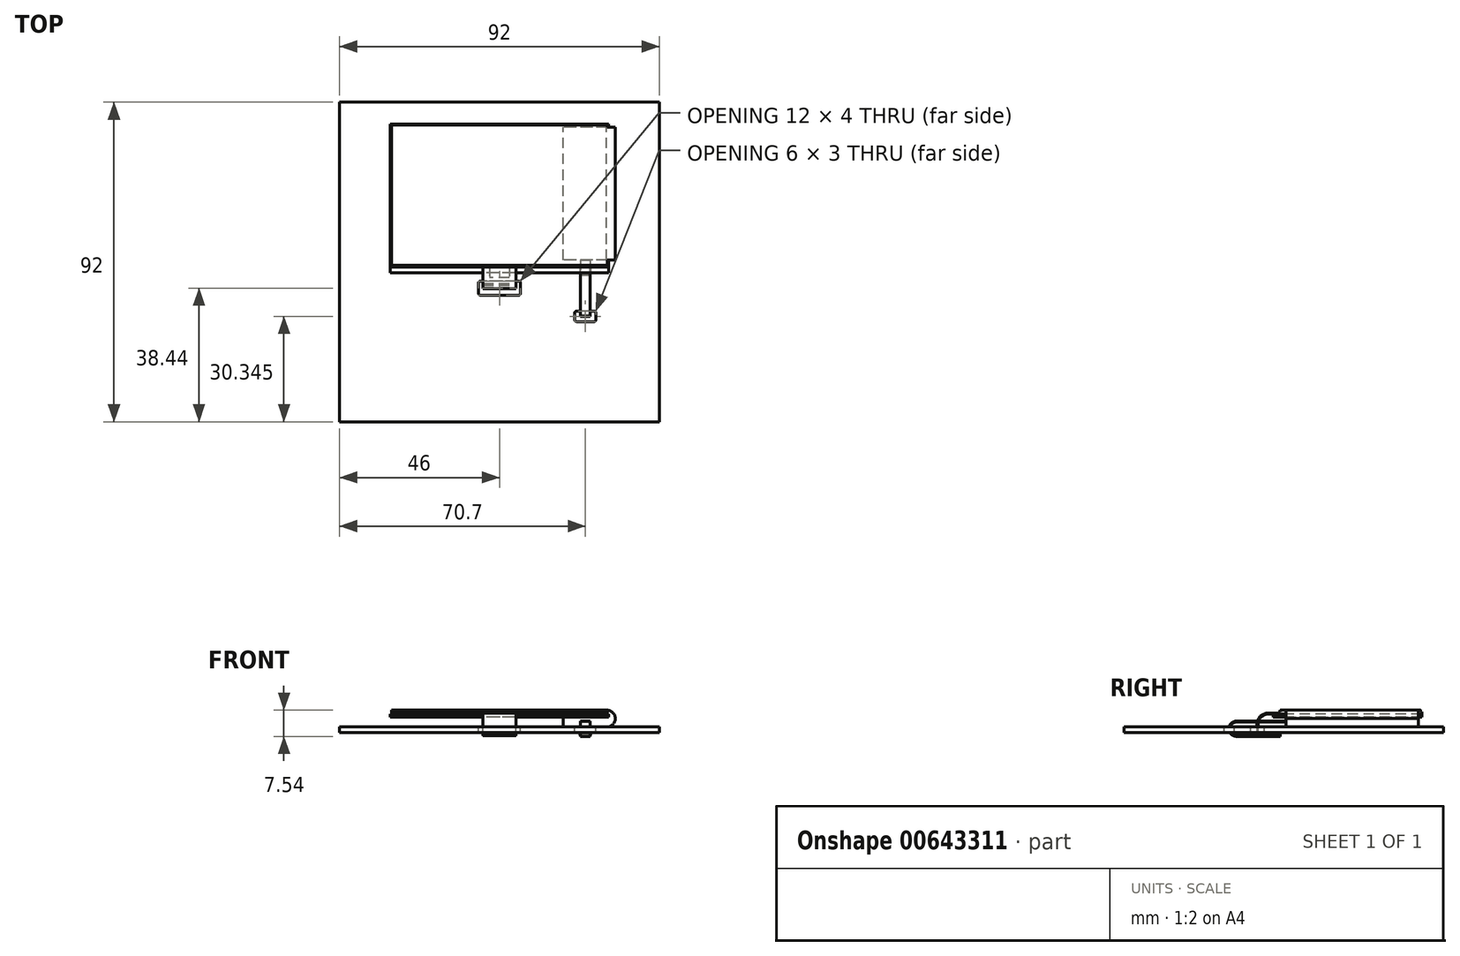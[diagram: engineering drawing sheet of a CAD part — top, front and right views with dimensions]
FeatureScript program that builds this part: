
annotation { "Feature Type Name" : "Feature", "Feature Type Description" : "" }
export const myFeature = defineFeature(function(context is Context, id is Id, definition is map)
    precondition{}
    {
        {
            var Q0;
            Q0=qCreatedBy(makeId("Top.planeOp"),FACE);
            var sketch = newSketch(context, id + "F0", { "sketchPlane" : qUnion([Q0])});
            skLineSegment(sketch, "E0.bottom", {"start": v(31.4, 21.41) * mm, "end": v(-31.4, 21.41) * mm});
            skLineSegment(sketch, "E0.top", {"start": v(31.4, -21.41) * mm, "end": v(-31.4, -21.41) * mm});
            skLineSegment(sketch, "E0.left", {"start": v(31.4, 21.41) * mm, "end": v(31.4, -21.41) * mm});
            skLineSegment(sketch, "E0.right", {"start": v(-31.4, 21.41) * mm, "end": v(-31.4, -21.41) * mm});
            skPoint(sketch, "E0.middle", {"position": v(0, 0) * mm});
            skSolve(sketch);
        }
        {
            var Q0;
            Q0=makeQuery(id+"F0.imprint","IMPRINT",FACE,{"disambiguationData":[TD([[makeQuery(id+"F0.imprint","IMPRINT",EDGE,{"derivedFrom":sQuery(id+"F0.wireOp",EDGE,"E0.bottom")}),1.0]])]});
            extrude(context, id + "F1", {"entities" : qUnion([Q0]), "depth" : (0.7 + 0.1) * mm, "offsetDistance" : 25 * mm});
        }
        {
            var Q0;
            Q0=makeQuery(id+"F1.opExtrude","CAP_FACE",FACE,{"disambiguationData":[OSD([sQuery(id+"F0.wireOp",EDGE,"E0.bottom"),sQuery(id+"F0.wireOp",EDGE,"E0.top"),sQuery(id+"F0.wireOp",EDGE,"E0.left"),sQuery(id+"F0.wireOp",EDGE,"E0.right")])],"isStart":true});
            var sketch = newSketch(context, id + "F2", { "sketchPlane" : qUnion([Q0])});
            skLineSegment(sketch, "E1.bottom", {"start": v(33.35, 17.74) * mm, "end": v(18.35, 17.74) * mm});
            skLineSegment(sketch, "E1.top", {"start": v(33.35, -20.41) * mm, "end": v(18.35, -20.41) * mm});
            skLineSegment(sketch, "E1.left", {"start": v(33.35, 17.74) * mm, "end": v(33.35, -20.41) * mm});
            skLineSegment(sketch, "E1.right", {"start": v(18.35, 17.74) * mm, "end": v(18.35, -20.41) * mm});
            skSolve(sketch);
        }
        {
            var Q0;
            Q0 = qSketchRegion(id + "F2", true);
            extrude(context, id + "F3", {"entities" : qUnion([Q0]), "operationType" : NewBodyOperationType.ADD, "depth" : 2.9 * mm, "offsetDistance" : 25 * mm});
        }
        {
            var Q0;
            {var subQ0=sQuery(id+"F0.wireOp",EDGE,"E0.right");var subQ1=sQuery(id+"F0.wireOp",EDGE,"E0.left");var subQ2=sQuery(id+"F0.wireOp",EDGE,"E0.top");var subQ3=sQuery(id+"F0.wireOp",EDGE,"E0.bottom");Q0=makeQuery(id+"FSjtb73LsPTqSAc_1.boolean.opBoolean","MERGE",FACE,{"derivedFrom":[makeQuery(id+"F1.opExtrude","CAP_FACE",FACE,{"disambiguationData":[OSD([subQ3,subQ2,subQ1,subQ0])],"isStart":false}),makeQuery(id+"FSjtb73LsPTqSAc_1.opExtrude","CAP_FACE",FACE,{"disambiguationData":[OSD([subQ3,subQ2,subQ1,subQ0])],"isStart":false})]});}
            var sketch = newSketch(context, id + "F4", { "sketchPlane" : qUnion([Q0])});
            skLineSegment(sketch, "E2.bottom", {"start": v(-31, 21.4) * mm, "end": v(31, 21.41) * mm});
            skLineSegment(sketch, "E2.top", {"start": v(-31, -19.81) * mm, "end": v(31, -19.81) * mm});
            skLineSegment(sketch, "E2.left", {"start": v(-31, 21.4) * mm, "end": v(-31, -19.81) * mm});
            skLineSegment(sketch, "E2.right", {"start": v(31, 21.41) * mm, "end": v(31, -19.81) * mm});
            skLineSegment(sketch, "E3", {"start": v(0, 21.4) * mm, "end": v(0, -19.81) * mm, "construction": true});
            skSolve(sketch);
        }
        {
            var Q0;
            Q0=makeQuery(id+"F4.imprint","IMPRINT",FACE,{"disambiguationData":[TD([[makeQuery(id+"F4.imprint","IMPRINT",EDGE,{"derivedFrom":sQuery(id+"F4.wireOp",EDGE,"E2.bottom")}),1.0]])]});
            extrude(context, id + "F5", {"entities" : qUnion([Q0]), "operationType" : NewBodyOperationType.ADD, "depth" : 0.6 * mm, "offsetDistance" : 25 * mm});
        }
        {
            var Q0;
            Q0=makeQuery(id+"F5.opExtrude","CAP_FACE",FACE,{"disambiguationData":[OSD([sQuery(id+"F4.wireOp",EDGE,"E2.bottom"),sQuery(id+"F4.wireOp",EDGE,"E2.top"),sQuery(id+"F4.wireOp",EDGE,"E2.left"),sQuery(id+"F4.wireOp",EDGE,"E2.right")])],"isStart":false});
            var sketch = newSketch(context, id + "F6", { "sketchPlane" : qUnion([Q0])});
            skLineSegment(sketch, "E4.bottom", {"start": v(-31, 21.11) * mm, "end": v(31, 21.11) * mm});
            skLineSegment(sketch, "E4.top", {"start": v(-31, -19.31) * mm, "end": v(31, -19.31) * mm});
            skLineSegment(sketch, "E4.left", {"start": v(-31, 21.11) * mm, "end": v(-31, -19.31) * mm});
            skLineSegment(sketch, "E4.right", {"start": v(31, 21.11) * mm, "end": v(31, -19.31) * mm});
            skLineSegment(sketch, "E5", {"start": v(0, 21.11) * mm, "end": v(0, -19.31) * mm, "construction": true});
            skSolve(sketch);
        }
        {
            var Q0;
            Q0=makeQuery(id+"F6.imprint","IMPRINT",FACE,{"disambiguationData":[TD([[makeQuery(id+"F6.imprint","IMPRINT",EDGE,{"derivedFrom":sQuery(id+"F6.wireOp",EDGE,"E4.bottom")}),-1.0]])]});
            extrude(context, id + "F7", {"entities" : qUnion([Q0]), "operationType" : NewBodyOperationType.ADD, "depth" : (1.95 - 1.41) * mm, "offsetDistance" : 25 * mm});
        }
        {
            var Q0;
            Q0=makeQuery(id+"F7.opExtrude","CAP_FACE",FACE,{"disambiguationData":[OSD([sQuery(id+"F6.wireOp",EDGE,"E4.bottom"),sQuery(id+"F6.wireOp",EDGE,"E4.top"),sQuery(id+"F6.wireOp",EDGE,"E4.left"),sQuery(id+"F6.wireOp",EDGE,"E4.right")])],"isStart":false});
            var sketch = newSketch(context, id + "F8", { "sketchPlane" : qUnion([Q0])});
            skLineSegment(sketch, "E6.bottom", {"start": v(33.35, 20.41) * mm, "end": v(-31, 20.4) * mm});
            skLineSegment(sketch, "E6.top", {"start": v(33.35, -17.74) * mm, "end": v(-31, -17.74) * mm});
            skLineSegment(sketch, "E6.left", {"start": v(-31, 20.41) * mm, "end": v(-31, -17.74) * mm});
            skLineSegment(sketch, "E6.right", {"start": v(33.35, 20.41) * mm, "end": v(33.35, -17.74) * mm});
            skSolve(sketch);
        }
        {
            var Q0;
            Q0=makeQuery(id+"F8.imprint","IMPRINT",FACE,{"disambiguationData":[TD([[makeQuery(id+"F8.imprint","IMPRINT",EDGE,{"derivedFrom":sQuery(id+"F8.wireOp",EDGE,"E6.bottom")}),1.0]])]});
            var Q1;
            Q1=makeQuery(id+"F3.opExtrude","CAP_FACE",FACE,{"disambiguationData":[OSD([sQuery(id+"F2.wireOp",EDGE,"E1.bottom"),sQuery(id+"F2.wireOp",EDGE,"E1.top"),sQuery(id+"F2.wireOp",EDGE,"E1.left"),sQuery(id+"F2.wireOp",EDGE,"E1.right")])],"isStart":true});
            extrude(context, id + "F9", {"entities" : qUnion([Q0]), "operationType" : NewBodyOperationType.ADD, "endBound" : BoundingType.UP_TO_SURFACE, "oppositeDirection" : true, "depth" : 25 * mm, "endBoundEntityFace" : qUnion([Q1]), "offsetDistance" : 25 * mm});
        }
        {
            var Q0;
            Q0=makeQuery(id+"F9.opExtrude","CAP_EDGE",EDGE,{"disambiguationData":[OSD([sQuery(id+"F8.wireOp",EDGE,"E6.right")])],"isStart":true});
            var Q1;
            Q1=makeQuery(id+"F3.opExtrude","CAP_EDGE",EDGE,{"disambiguationData":[OSD([sQuery(id+"F2.wireOp",EDGE,"E1.left")])],"isStart":false});
            fillet(context, id + "F10", {"entities" : qUnion([Q0, Q1]), "radius" : 2.5 * mm, "tangentPropagation" : true, "allowEdgeOverflow" : false});
        }
        {
            var Q0;
            Q0=makeQuery(id+"F9.boolean.opBoolean","MERGE",FACE,{"derivedFrom":[makeQuery(id+"F3.opExtrude","SWEPT_FACE",FACE,{"disambiguationData":[OSD([sQuery(id+"F2.wireOp",EDGE,"E1.bottom")])]}),makeQuery(id+"F9.opExtrude","SWEPT_FACE",FACE,{"disambiguationData":[OSD([sQuery(id+"F8.wireOp",EDGE,"E6.top")])]})]});
            var sketch = newSketch(context, id + "F11", { "sketchPlane" : qUnion([Q0])});
            skLineSegment(sketch, "E7.bottom", {"start": v(23.3, -1.2) * mm, "end": v(26.1, -1.2) * mm});
            skLineSegment(sketch, "E7.top", {"start": v(23.3, -1.5) * mm, "end": v(26.1, -1.5) * mm});
            skLineSegment(sketch, "E7.left", {"start": v(23.3, -1.2) * mm, "end": v(23.3, -1.5) * mm});
            skLineSegment(sketch, "E7.right", {"start": v(26.1, -1.2) * mm, "end": v(26.1, -1.5) * mm});
            skPoint(sketch, "E8", {"position": v(24.7, -1.35) * mm});
            skLineSegment(sketch, "E9", {"start": v(24.7, -1.2) * mm, "end": v(24.7, -1.35) * mm, "construction": true});
            skLineSegment(sketch, "E10", {"start": v(24.7, -1.35) * mm, "end": v(26.1, -1.35) * mm, "construction": true});
            skSolve(sketch);
        }
        {
            var Q0;
            Q0=makeQuery(id+"F5.opExtrude","SWEPT_FACE",FACE,{"disambiguationData":[OSD([sQuery(id+"F4.wireOp",EDGE,"E2.top")])]});
            var sketch = newSketch(context, id + "F12", { "sketchPlane" : qUnion([Q0])});
            skLineSegment(sketch, "E11.bottom", {"start": v(4.75, 1.1) * mm, "end": v(-4.75, 1.1) * mm});
            skLineSegment(sketch, "E11.top", {"start": v(4.75, 0.81) * mm, "end": v(-4.75, 0.8) * mm});
            skLineSegment(sketch, "E11.left", {"start": v(4.75, 1.1) * mm, "end": v(4.75, 0.8) * mm});
            skLineSegment(sketch, "E11.right", {"start": v(-4.75, 1.1) * mm, "end": v(-4.75, 0.81) * mm});
            skPoint(sketch, "E11.middle", {"position": v(0, 0.96) * mm});
            skPoint(sketch, "E11.middle.positionSnap0", {"position": v(0, 0.8) * mm});
            skPoint(sketch, "E11.centerSnap0", {"position": v(0, 0.8) * mm});
            skSolve(sketch);
        }
        {
            var Q0;
            Q0=makeQuery(id+"F3.opExtrude","CAP_FACE",FACE,{"disambiguationData":[OSD([sQuery(id+"F2.wireOp",EDGE,"E1.bottom"),sQuery(id+"F2.wireOp",EDGE,"E1.top"),sQuery(id+"F2.wireOp",EDGE,"E1.left"),sQuery(id+"F2.wireOp",EDGE,"E1.right")])],"isStart":false});
            var sketch = newSketch(context, id + "F13", { "sketchPlane" : qUnion([Q0])});
            skLineSegment(sketch, "E12.bottom", {"start": v(46, 64.33) * mm, "end": v(-46, 64.33) * mm});
            skLineSegment(sketch, "E12.top", {"start": v(46, -27.67) * mm, "end": v(-46, -27.67) * mm});
            skLineSegment(sketch, "E12.left", {"start": v(46, 64.33) * mm, "end": v(46, -27.67) * mm});
            skLineSegment(sketch, "E12.right", {"start": v(-46, 64.33) * mm, "end": v(-46, -27.67) * mm});
            skPoint(sketch, "E12.middle", {"position": v(0, 64.33) * mm});
            skSolve(sketch);
        }
        {
            var Q0;
            Q0 = qSketchRegion(id + "F13", true);
            extrude(context, id + "F14", {"entities" : qUnion([Q0]), "depth" : 1.6 * mm, "offsetDistance" : 25 * mm});
        }
        {
            var Q0;
            Q0=makeQuery(id+"F14.opExtrude","CAP_FACE",FACE,{"disambiguationData":[OSD([sQuery(id+"F13.wireOp",EDGE,"E12.bottom"),sQuery(id+"F13.wireOp",EDGE,"E12.top"),sQuery(id+"F13.wireOp",EDGE,"E12.left"),sQuery(id+"F13.wireOp",EDGE,"E12.right")])],"isStart":false});
            var sketch = newSketch(context, id + "F15", { "sketchPlane" : qUnion([Q0])});
            skPoint(sketch, "E13", {"position": v(24.7, 21.74) * mm});
            skSolve(sketch);
        }
        {
            var Q0;
            {var subQ3=sQuery(id+"F13.wireOp",EDGE,"E12.bottom");Q0=makeQuery(id+"F15.imprint","IMPRINT",FACE,{"disambiguationData":[TD([[makeQuery(id+"F15.imprint","IMPRINT",EDGE,{"derivedFrom":makeQuery(id+"F14.opExtrude","CAP_EDGE",EDGE,{"disambiguationData":[OSD([subQ3])],"isStart":false})}),1.0]])]});}
            var sketch = newSketch(context, id + "F16", { "sketchPlane" : qUnion([Q0])});
            skLineSegment(sketch, "E14.bottom", {"start": v(26.2, 19.35) * mm, "end": v(23.2, 19.35) * mm});
            skLineSegment(sketch, "E14.top", {"start": v(26.2, 22.25) * mm, "end": v(23.2, 22.25) * mm});
            skLineSegment(sketch, "E14.left", {"start": v(26.2, 19.35) * mm, "end": v(26.2, 22.25) * mm});
            skLineSegment(sketch, "E14.right", {"start": v(23.2, 19.35) * mm, "end": v(23.2, 22.25) * mm});
            skPoint(sketch, "E14.middle", {"position": v(24.7, 20.8) * mm});
            skSolve(sketch);
        }
        {
            var Q0;
            Q0=makeQuery(id+"F16.imprint","IMPRINT",FACE,{"disambiguationData":[TD([[makeQuery(id+"F16.imprint","IMPRINT",EDGE,{"derivedFrom":sQuery(id+"F16.wireOp",EDGE,"E14.bottom")}),-1.0]])]});
            extrude(context, id + "F17", {"entities" : qUnion([Q0]), "operationType" : NewBodyOperationType.ADD, "depth" : 0.79 * mm, "offsetDistance" : 25 * mm});
        }
        {
            var Q0;
            Q0=makeQuery(id+"F14.opExtrude","SWEPT_FACE",FACE,{"disambiguationData":[OSD([sQuery(id+"F13.wireOp",EDGE,"E12.right")])]});
            cPlane(context, id + "F18", {"entities" : qUnion([Q0]), "cplaneType" : CPlaneType.OFFSET, "offset" : (70.7) * mm, "oppositeDirection" : true, "width" : 150 * mm, "height" : 150 * mm});
        }
        {
            var Q0;
            Q0=qCreatedBy(id+"F18.planeOp",FACE);
            var sketch = newSketch(context, id + "F19", { "sketchPlane" : qUnion([Q0])});
            skLineSegment(sketch, "E15", {"start": v(17.74, -1.35) * mm, "end": v(31.94, -1.35) * mm});
            skArc(sketch, "E16", {"start": v(31.94, -5.44) * mm, "mid": v(33.98, -3.4) * mm, "end": v(31.94, -1.35) * mm});
            skLineSegment(sketch, "E17", {"start": v(31.94, -5.44) * mm, "end": v(19.35, -5.44) * mm});
            skSolve(sketch);
        }
        {
            var Q0;
            Q0 = qSketchRegion(id + "F11", true);
            var Q1;
            Q1 = qConstructionFilter(qBodyType(qCreatedBy(id + "F19" ,EDGE), BodyType.WIRE), ConstructionObject.NO);
            sweep(context, id + "F20", {"operationType" : NewBodyOperationType.ADD, "profiles" : qUnion([Q0]), "path" : qUnion([Q1])});
        }
        {
            var Q0;
            Q0=makeQuery(id+"F14.opExtrude","CAP_FACE",FACE,{"disambiguationData":[OSD([sQuery(id+"F13.wireOp",EDGE,"E12.bottom"),sQuery(id+"F13.wireOp",EDGE,"E12.top"),sQuery(id+"F13.wireOp",EDGE,"E12.left"),sQuery(id+"F13.wireOp",EDGE,"E12.right")])],"isStart":true});
            var sketch = newSketch(context, id + "F21", { "sketchPlane" : qUnion([Q0])});
            skLineSegment(sketch, "E18.bottom", {"start": v(27.3, -32.48) * mm, "end": v(22.1, -32.48) * mm});
            skLineSegment(sketch, "E18.top", {"start": v(27.3, -35.48) * mm, "end": v(22.1, -35.48) * mm});
            skLineSegment(sketch, "E18.left", {"start": v(27.7, -32.88) * mm, "end": v(27.7, -35.08) * mm});
            skLineSegment(sketch, "E18.right", {"start": v(21.7, -32.88) * mm, "end": v(21.7, -35.08) * mm});
            skPoint(sketch, "E18.middle", {"position": v(24.7, -33.98) * mm});
            skPoint(sketch, "E19.visualSharp", {"position": v(21.7, -32.48) * mm});
            skArc(sketch, "E19.filletArc", {"start": v(22.1, -32.48) * mm, "mid": v(21.82, -32.6) * mm, "end": v(21.7, -32.88) * mm});
            skPoint(sketch, "E20.visualSharp", {"position": v(27.7, -32.48) * mm});
            skArc(sketch, "E20.filletArc", {"start": v(27.7, -32.88) * mm, "mid": v(27.58, -32.6) * mm, "end": v(27.3, -32.48) * mm});
            skPoint(sketch, "E21.visualSharp", {"position": v(27.7, -35.48) * mm});
            skArc(sketch, "E21.filletArc", {"start": v(27.3, -35.48) * mm, "mid": v(27.58, -35.37) * mm, "end": v(27.7, -35.08) * mm});
            skPoint(sketch, "E22.visualSharp", {"position": v(21.7, -35.48) * mm});
            skArc(sketch, "E22.filletArc", {"start": v(21.7, -35.08) * mm, "mid": v(21.82, -35.37) * mm, "end": v(22.1, -35.48) * mm});
            skSolve(sketch);
        }
        {
            var Q0;
            Q0 = qSketchRegion(id + "F21", true);
            var Q1;
            Q1=makeQuery(id+"F14.opExtrude","CAP_FACE",FACE,{"disambiguationData":[OSD([sQuery(id+"F13.wireOp",EDGE,"E12.bottom"),sQuery(id+"F13.wireOp",EDGE,"E12.top"),sQuery(id+"F13.wireOp",EDGE,"E12.left"),sQuery(id+"F13.wireOp",EDGE,"E12.right")])],"isStart":false});
            extrude(context, id + "F22", {"entities" : qUnion([Q0]), "operationType" : NewBodyOperationType.REMOVE, "endBound" : BoundingType.UP_TO_SURFACE, "oppositeDirection" : true, "depth" : 25 * mm, "endBoundEntityFace" : qUnion([Q1]), "offsetDistance" : 25 * mm});
        }
        {
            var Q0;
            Q0=makeQuery(id+"F5.opExtrude","SWEPT_FACE",FACE,{"disambiguationData":[OSD([sQuery(id+"F4.wireOp",EDGE,"E2.top")])]});
            var sketch = newSketch(context, id + "F23", { "sketchPlane" : qUnion([Q0])});
            skLineSegment(sketch, "E23.bottom", {"start": v(4.75, 0.81) * mm, "end": v(-4.75, 0.8) * mm});
            skLineSegment(sketch, "E23.top", {"start": v(4.75, 1.11) * mm, "end": v(-4.75, 1.1) * mm});
            skLineSegment(sketch, "E23.left", {"start": v(4.75, 0.81) * mm, "end": v(4.75, 1.11) * mm});
            skLineSegment(sketch, "E23.right", {"start": v(-4.75, 0.8) * mm, "end": v(-4.75, 1.1) * mm});
            skPoint(sketch, "E23.middle", {"position": v(0, 0.96) * mm});
            skPoint(sketch, "E23.middle.positionSnap0", {"position": v(0, 0.8) * mm});
            skPoint(sketch, "E23.centerSnap0", {"position": v(0, 0.8) * mm});
            skSolve(sketch);
        }
        {
            var Q0;
            Q0=makeQuery(id+"F14.opExtrude","CAP_FACE",FACE,{"disambiguationData":[OSD([sQuery(id+"F13.wireOp",EDGE,"E12.bottom"),sQuery(id+"F13.wireOp",EDGE,"E12.top"),sQuery(id+"F13.wireOp",EDGE,"E12.left"),sQuery(id+"F13.wireOp",EDGE,"E12.right")])],"isStart":false});
            var sketch = newSketch(context, id + "F24", { "sketchPlane" : qUnion([Q0])});
            skLineSegment(sketch, "E24.bottom", {"start": v(2.8, 19.41) * mm, "end": v(-2.8, 19.41) * mm});
            skLineSegment(sketch, "E24.top", {"start": v(2.8, 22.81) * mm, "end": v(-2.8, 22.81) * mm});
            skLineSegment(sketch, "E24.left", {"start": v(2.8, 19.41) * mm, "end": v(2.8, 22.81) * mm});
            skLineSegment(sketch, "E24.right", {"start": v(-2.8, 19.41) * mm, "end": v(-2.8, 22.81) * mm});
            skPoint(sketch, "E24.middle", {"position": v(0, 21.11) * mm});
            skSolve(sketch);
        }
        {
            var Q0;
            Q0=makeQuery(id+"F24.imprint","IMPRINT",FACE,{"disambiguationData":[TD([[makeQuery(id+"F24.imprint","IMPRINT",EDGE,{"derivedFrom":sQuery(id+"F24.wireOp",EDGE,"E24.bottom")}),-1.0]])]});
            extrude(context, id + "F25", {"entities" : qUnion([Q0]), "operationType" : NewBodyOperationType.ADD, "depth" : 0.55 * mm, "offsetDistance" : 25 * mm});
        }
        {
            var Q0;
            Q0=makeQuery(id+"F14.opExtrude","SWEPT_FACE",FACE,{"disambiguationData":[OSD([sQuery(id+"F13.wireOp",EDGE,"E12.left")])]});
            cPlane(context, id + "F26", {"entities" : qUnion([Q0]), "cplaneType" : CPlaneType.OFFSET, "offset" : 46 * mm, "oppositeDirection" : true, "width" : 150 * mm, "height" : 150 * mm});
        }
        {
            var Q0;
            Q0=qCreatedBy(id+"F26.planeOp",FACE);
            var sketch = newSketch(context, id + "F27", { "sketchPlane" : qUnion([Q0])});
            skLineSegment(sketch, "E25", {"start": v(-19.81, 0.96) * mm, "end": v(-21.41, 0.96) * mm});
            skArc(sketch, "E26", {"start": v(-22.81, 0.96) * mm, "mid": v(-25.9, -2.12) * mm, "end": v(-22.81, -5.2) * mm});
            skLineSegment(sketch, "E27", {"start": v(-22.81, -5.2) * mm, "end": v(-19.41, -5.2) * mm});
            skLineSegment(sketch, "E28", {"start": v(-21.41, 0.96) * mm, "end": v(-22.81, 0.96) * mm});
            skSolve(sketch);
        }
        {
            var Q0;
            Q0=makeQuery(id+"F23.imprint","IMPRINT",FACE,{"disambiguationData":[TD([[makeQuery(id+"F23.imprint","IMPRINT",EDGE,{"derivedFrom":sQuery(id+"F23.wireOp",EDGE,"E23.bottom")}),1.0]])]});
            var Q1;
            Q1 = qConstructionFilter(qBodyType(qCreatedBy(id + "F27" ,EDGE), BodyType.WIRE), ConstructionObject.NO);
            sweep(context, id + "F28", {"operationType" : NewBodyOperationType.ADD, "profiles" : qUnion([Q0]), "path" : qUnion([Q1])});
        }
        {
            var Q0;
            Q0=makeQuery(id+"F14.opExtrude","CAP_FACE",FACE,{"disambiguationData":[OSD([sQuery(id+"F13.wireOp",EDGE,"E12.bottom"),sQuery(id+"F13.wireOp",EDGE,"E12.top"),sQuery(id+"F13.wireOp",EDGE,"E12.left"),sQuery(id+"F13.wireOp",EDGE,"E12.right")])],"isStart":true});
            var sketch = newSketch(context, id + "F29", { "sketchPlane" : qUnion([Q0])});
            skLineSegment(sketch, "E29.bottom", {"start": v(5.6, -23.9) * mm, "end": v(-5.6, -23.9) * mm});
            skLineSegment(sketch, "E29.top", {"start": v(5.6, -27.9) * mm, "end": v(-5.6, -27.9) * mm});
            skLineSegment(sketch, "E29.left", {"start": v(6, -24.3) * mm, "end": v(6, -27.5) * mm});
            skLineSegment(sketch, "E29.right", {"start": v(-6, -24.3) * mm, "end": v(-6, -27.5) * mm});
            skPoint(sketch, "E29.middle", {"position": v(0, -25.9) * mm});
            skPoint(sketch, "E30.visualSharp", {"position": v(-6, -23.9) * mm});
            skArc(sketch, "E30.filletArc", {"start": v(-5.6, -23.9) * mm, "mid": v(-5.88, -24) * mm, "end": v(-6, -24.3) * mm});
            skPoint(sketch, "E31.visualSharp", {"position": v(6, -23.9) * mm});
            skArc(sketch, "E31.filletArc", {"start": v(6, -24.3) * mm, "mid": v(5.88, -24) * mm, "end": v(5.6, -23.9) * mm});
            skPoint(sketch, "E32.visualSharp", {"position": v(6, -27.9) * mm});
            skArc(sketch, "E32.filletArc", {"start": v(5.6, -27.9) * mm, "mid": v(5.88, -27.77) * mm, "end": v(6, -27.5) * mm});
            skPoint(sketch, "E33.visualSharp", {"position": v(-6, -27.9) * mm});
            skArc(sketch, "E33.filletArc", {"start": v(-6, -27.5) * mm, "mid": v(-5.88, -27.77) * mm, "end": v(-5.6, -27.9) * mm});
            skSolve(sketch);
        }
        {
            var Q0;
            Q0=makeQuery(id+"F29.imprint","IMPRINT",FACE,{"disambiguationData":[TD([[makeQuery(id+"F29.imprint","IMPRINT",EDGE,{"derivedFrom":sQuery(id+"F29.wireOp",EDGE,"E29.bottom")}),1.0]])]});
            var Q1;
            Q1=makeQuery(id+"F14.opExtrude","CAP_FACE",FACE,{"disambiguationData":[OSD([sQuery(id+"F13.wireOp",EDGE,"E12.bottom"),sQuery(id+"F13.wireOp",EDGE,"E12.top"),sQuery(id+"F13.wireOp",EDGE,"E12.left"),sQuery(id+"F13.wireOp",EDGE,"E12.right")])],"isStart":false});
            extrude(context, id + "F30", {"entities" : qUnion([Q0]), "operationType" : NewBodyOperationType.REMOVE, "endBound" : BoundingType.UP_TO_SURFACE, "oppositeDirection" : true, "depth" : 25 * mm, "endBoundEntityFace" : qUnion([Q1]), "offsetDistance" : 25 * mm});
        }
    });
